# Revit family: LRTP 2x2_2x4
name_source: partatom
category: Lighting Fixtures
units: mm (PartAtom-declared; Revit-internal decimal feet)

## family parameters
Always vertical = Yes
Cut with Voids When Loaded = No
Host = Ceiling
Light Source = Yes
OmniClass Number = 23.80.70.11.14.17
OmniClass Title = Direct/Indirect
Part Type = Normal
Room Calculation Point = No
Round Connector Dimension = Use Diameter
Shared = No

## types (7) — shared parameters
Assembly Code = D5020200
Color Filter = 16777215
Description = LED Recessed Troffer Type P
Dimming Lamp Color Temperature Shift = <None>
Emit Shape Visible in Rendering = No
Emit from Rectangle Width = 1' - 11 3/4"
Housing Finish = Metal - Viscor - White
Lamp = LED
Lens Finish = Polycarbonate - Viscor - Frosted Round
Manufacturer = VISIONEERING by VISCOR
Model = LRTP
Reflector Width = 0' - 11 7/8"
Tilt Angle = 90.00°
URL = https://www.viscor.com
Voltage = 120 V
Width = 1' - 11 3/4"

## per-type parameters (varying)
| type | Apparent Load | Emit from Rectangle Length | Lamp Wattage | Length | Photometric Web File |
| LRTP2X2-LED840K027LUNV | 23 VA | 1' - 11 3/4" | 23 VA | 1' - 11 3/4" | LRTP2X2-LED840K027LUNV-G002079.IES |
| LRTP2x4-LED840K042LUNV | 31 VA | 3' - 11 3/4" | 31 VA | 3' - 11 3/4" | LRTP2X4-LED840K042LUNV-G002081.IES |
| LRTP2x4-LED840K037LUNV | 25 VA | 3' - 11 3/4" | 25 VA | 3' - 11 3/4" | LRTP2X4-LED840K037LUNV-G002085.IES |
| LRTP2X2-LED840K035LUNV | 30 VA | 1' - 11 3/4" | 30 VA | 1' - 11 3/4" | LRTP2X2-LED840K035LUNV-G002087.IES |
| LRTP2X2-LED840K040LUNV | 32 VA | 1' - 11 3/4" | 32 VA | 1' - 11 3/4" | LRTP2X2-LED840K040LUNV-G002051.IES |
| LRTP2X4-LED840K050LUNV | 39 VA | 3' - 11 3/4" | 39 VA | 3' - 11 3/4" | LRTP2X4-LED840K050LUNV-G002082.IES |
| LRTP2X4-LED840K061LUNV | 43 VA | 3' - 11 3/4" | 43 VA | 3' - 11 3/4" | LRTP2X4-LED840K061LUNV-G002084.IES |

## geometry (parser evidence)
native form markers: Sweep x3
no freeform markers — native parametric forms only
